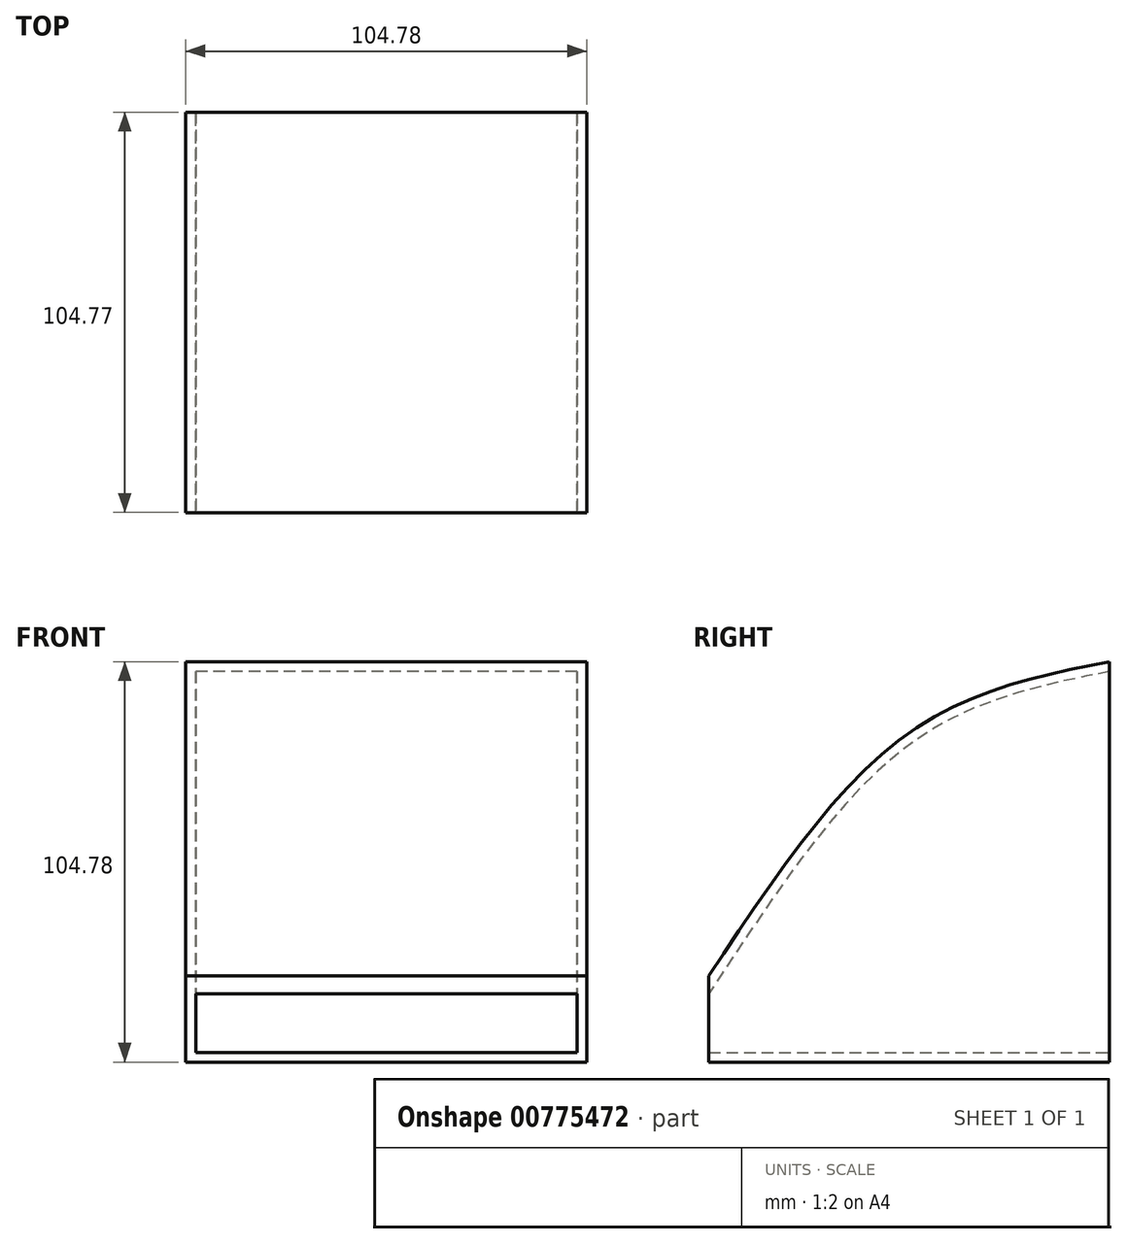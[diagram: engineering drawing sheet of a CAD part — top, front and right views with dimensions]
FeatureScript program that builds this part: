
annotation { "Feature Type Name" : "Feature", "Feature Type Description" : "" }
export const myFeature = defineFeature(function(context is Context, id is Id, definition is map)
    precondition{}
    {
        {
            var Q0;
            Q0=qCreatedBy(makeId("Right.planeOp"),FACE);
            var sketch = newSketch(context, id + "F0", { "sketchPlane" : qUnion([Q0])});
            skLineSegment(sketch, "E0", {"start": v(12.45, 0) * mm, "end": v(117.22, 0) * mm});
            skLineSegment(sketch, "E1", {"start": v(117.22, 0) * mm, "end": v(117.22, 104.78) * mm});
            skLineSegment(sketch, "E2", {"start": v(12.45, 22.52) * mm, "end": v(12.45, 0) * mm});
            skFitSpline(sketch, "E3", {"points": [v(117.22, 104.78) * mm, v(65.12, 86.4) * mm, v(12.45, 22.52) * mm], "startDerivative": vector(-120.41, -23.96) * mm, "endDerivative": vector(-90.15, -136.75) * mm});
            skSolve(sketch);
        }
        {
            var Q0;
            Q0=makeQuery(id+"F0.imprint","IMPRINT",FACE,{"disambiguationData":[TD([[makeQuery(id+"F0.imprint","IMPRINT",EDGE,{"derivedFrom":sQuery(id+"F0.wireOp",EDGE,"E0")}),1.0]])]});
            extrude(context, id + "F1", {"entities" : qUnion([Q0]), "depth" : 104.77 * mm, "offsetDistance" : 25.4 * mm});
        }
        {
            var Q0;
            Q0=makeQuery(id+"F1.opExtrude","SWEPT_FACE",FACE,{"disambiguationData":[OSD([sQuery(id+"F0.wireOp",EDGE,"E1")])]});
            var Q1;
            Q1=makeQuery(id+"F1.opExtrude","SWEPT_FACE",FACE,{"disambiguationData":[OSD([sQuery(id+"F0.wireOp",EDGE,"E2")])]});
            shell(context, id + "F2", {"entities" : qUnion([Q0, Q1]), "thickness" : 2.54 * mm});
        }
    });
